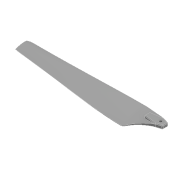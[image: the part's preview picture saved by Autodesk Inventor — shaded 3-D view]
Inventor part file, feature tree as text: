
AUTODESK INVENTOR PART (.ipt)
format: ipt  version: 2022 (Build 260153000, 153)  size: 259,072 bytes
history: native  units: in
note: dims shown in document units (in); Inventor stores cm internally (conversion verified against a paired STEP export)
features: extrude x1, sketch x1, fillet x1
ambient origin geometry x8: Origin, YZ Plane, XZ Plane, XY Plane, X Axis, Y Axis, Z Axis, Center Point
bodies: Solid1 (feature_tree)
feature tree (3):
  extrude  "Extrusion1"  [1 undecoded]
  sketch  "Sketch1"  dims[d0=0.1732in d1=0.0in]
  fillet  "Fillet1"  [1 undecoded]
note: 2 required parameter values undecoded (feature->parameter linkage not recoverable at this tier; creation-order binding heuristic only, values carry confidence <= 0.55)
